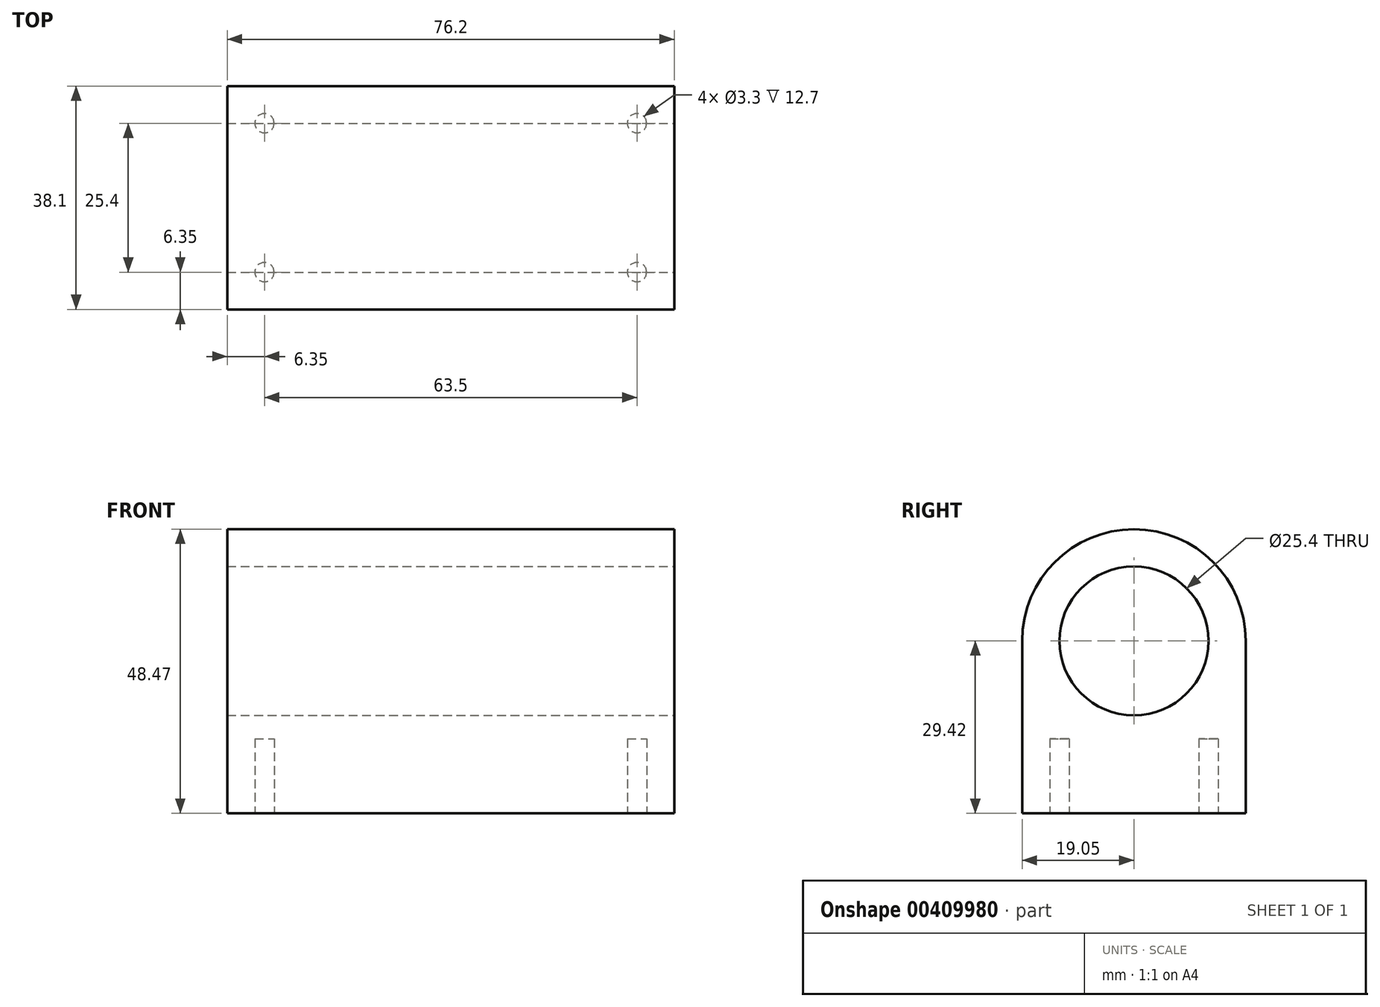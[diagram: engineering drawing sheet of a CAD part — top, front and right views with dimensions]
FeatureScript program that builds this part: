
annotation { "Feature Type Name" : "Feature", "Feature Type Description" : "" }
export const myFeature = defineFeature(function(context is Context, id is Id, definition is map)
    precondition{}
    {
        {
            var Q0;
            Q0=qCreatedBy(makeId("Right.planeOp"),FACE);
            var sketch = newSketch(context, id + "F0", { "sketchPlane" : qUnion([Q0])});
            skCircle(sketch, "E0", {"center": v(0, 0) * mm, "radius": 12.7 * mm});
            skArc(sketch, "E1", {"start": v(19.05, 0) * mm, "mid": v(0, 19.05) * mm, "end": v(-19.05, 0) * mm});
            skLineSegment(sketch, "E2", {"start": v(-19.05, 0) * mm, "end": v(-19.05, -29.42) * mm});
            skLineSegment(sketch, "E3", {"start": v(-19.05, -29.42) * mm, "end": v(19.05, -29.42) * mm});
            skLineSegment(sketch, "E4", {"start": v(19.05, -29.42) * mm, "end": v(19.05, 0) * mm});
            skSolve(sketch);
        }
        {
            var Q0;
            Q0=makeQuery(id+"F0.imprint","IMPRINT",FACE,{"disambiguationData":[TD([[makeQuery(id+"F0.imprint","IMPRINT",EDGE,{"derivedFrom":sQuery(id+"F0.wireOp",EDGE,"E0")}),-1.0]])]});
            extrude(context, id + "F1", {"entities" : qUnion([Q0]), "endBound" : BoundingType.SYMMETRIC, "oppositeDirection" : true, "depth" : 76.2 * mm});
        }
        {
            var Q0;
            Q0=makeQuery(id+"F1.opExtrude","SWEPT_FACE",FACE,{"disambiguationData":[OSD([sQuery(id+"F0.wireOp",EDGE,"E3")])]});
            var sketch = newSketch(context, id + "F2", { "sketchPlane" : qUnion([Q0])});
            skLineSegment(sketch, "E5", {"start": v(12.72, 0) * mm, "end": v(-85.5, 0) * mm, "construction": true});
            skCircle(sketch, "E6", {"center": v(31.75, 12.7) * mm, "radius": 1.65 * mm});
            skCircle(sketch, "E7", {"center": v(-31.75, 12.7) * mm, "radius": 1.65 * mm});
            skCircle(sketch, "E8.MirrorC", {"center": v(-31.75, -12.7) * mm, "radius": 1.65 * mm});
            skCircle(sketch, "E9.MirrorC", {"center": v(31.75, -12.7) * mm, "radius": 1.65 * mm});
            skSolve(sketch);
        }
        {
            var Q0;
            Q0 = qSketchRegion(id + "F2", true);
            extrude(context, id + "F3", {"entities" : qUnion([Q0]), "operationType" : NewBodyOperationType.REMOVE, "oppositeDirection" : true, "depth" : 12.7 * mm});
        }
    });
